# Revit family: STS-622 IP-громкоговоритель_RV17_LOD400
name_source: partatom
category: Устройства вызова и оповещения
revit_build: Autodesk Revit 2017 (Build: 20170118_1100(x64)
units: mm (PartAtom-declared; Revit-internal decimal feet)

## family parameters
Всегда вертикально = Нет
На основе рабочей плоскости = Нет
Общий = Нет
При загрузке вырезать с полостями = Нет
Размер круглого соединителя = Использовать диаметр
Сохранять ориентацию аннотаций = Нет
Тип детали = Нормальный
Точка расчета площади = Нет

## types (1)
- STS-622 IP-громкоговоритель
    ADSK_URL страницы изделия = https://stilsoft.ru
    ADSK_Единица измерения = шт.
    ADSK_Завод-изготовитель = ООО «Основа Безопасности»
    ADSK_Количество = 1
    ADSK_Марка = СТВФ.422334.012
    ADSK_Масса = 2.05
    ADSK_Наименование = IP-громкоговоритель STS-622
    ADSK_Размер_Высота = 205 мм
    ADSK_Размер_Длина = 310 мм
    ADSK_Размер_Ширина = 282 мм
    d_короба = 20 мм
    Диапазон рабочих температур, °С = от – 50 до + 50
    Коэффициент нелинейных искажений на частоте 1000 Гц, не более, % = 5
    Напряжение электропитания = РоЕ
    Потребляемая мощность, не более, Вт = 30
    Режим работы = круглосуточный
    Стандарт РоЕ = IEEE 802.3 af
    Стандарт интерфейса связи = 10 / 100 Base-T Ethernet
    Уровень звука речевых сообщений в любой точке озвучивания пространства, не более, не менее, дБ = 120
    Уровень звука речевых сообщений на расстоянии 3 метров от специального = 75
